# Revit family: KOMFORT EC SB L R
name_source: partatom
category: Оборудование
units: mm (PartAtom-declared; Revit-internal decimal feet)

## family parameters
Всегда вертикально = Да
Классификация = Нет
На основе рабочей плоскости = Нет
Общий = Нет
При загрузке вырезать с полостями = Нет
Размер круглого соединителя = Использовать диаметр
Тип детали = Нормальный
Точка принадлежности помещению = Нет

## types (8) — shared parameters
00_20_Manufacturer = Blauberg
00_20_Name = Air handling unit
B = 568 мм
B2 = 181 мм
B6 = 421 мм
B7 = 101 мм
Casing Material = Metal, painted, white, matt
D = 160 мм
Diameter = 160 мм
Dy = 150 мм
Filter = G4
Frequency = 50 Гц
H = 1044 мм
Height = 1094 мм
L = 560 мм
Length = 560 мм
Load Classification = HVAC
Maintenance zone material = <По категории>
Maximum Air Flow = 390.0 м³/ч
Number of Fase = 1
Sound pressure level at 3 m distance = 35 dBA
Temperature of moving air = -25...+40°С
URL = https://blaubergventilatoren.de
Voltage = 230 В
Weight = 66.00 кг
Width = 568 мм
b1 = 212 мм
h1 = 1094 мм
l1 = 390 мм
Изготовитель = Blauberg
zero-valued in all types: Отметка по умолчанию

## per-type parameters (varying)
| type | Amperage | Apparent Load | B1 | B3 | B4 | B5 | B8 | Power |
| KOMFORT EC SB 250 R S21 | 1 А | 315 В·А | 308 мм | 464 мм | 290 мм | 110 мм | 101 мм | 180 Вт |
| KOMFORT EC SB 250 L S21 | 1 А | 315 В·А | 411 мм | 96 мм | 270 мм | 450 мм | 459 мм | 180 Вт |
| KOMFORT EC SBE 250 L S21 | 7 А | 1716 В·А | 411 мм | 96 мм | 270 мм | 450 мм | 459 мм | 1580 Вт |
| KOMFORT EC SBE 250 R S21 | 7 А | 1716 В·А | 308 мм | 464 мм | 290 мм | 110 мм | 101 мм | 1580 Вт |
| KOMFORT EC SB 250-E L S21 | 1 А | 315 В·А | 411 мм | 96 мм | 270 мм | 450 мм | 459 мм | 180 Вт |
| KOMFORT EC SB 250-E R S21 | 1 А | 315 В·А | 308 мм | 464 мм | 290 мм | 110 мм | 101 мм | 180 Вт |
| KOMFORT EC SBE 250-E L S21 | 7 А | 1716 В·А | 411 мм | 96 мм | 270 мм | 450 мм | 459 мм | 1580 Вт |
| KOMFORT EC SBE 250-E R S21 | 7 А | 1716 В·А | 308 мм | 464 мм | 290 мм | 110 мм | 101 мм | 1580 Вт |

note: column(s) folded — value = type name in every type: 00_20_Type
